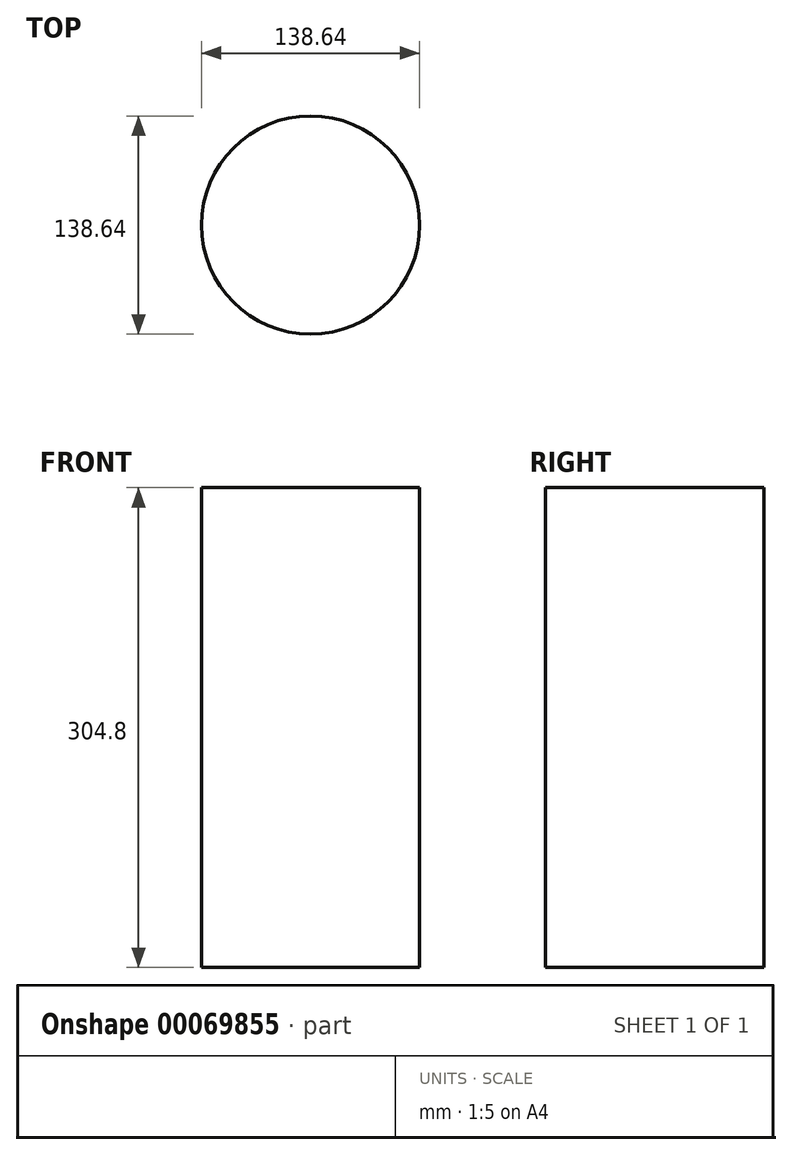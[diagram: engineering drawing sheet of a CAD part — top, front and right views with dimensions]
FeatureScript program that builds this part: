
annotation { "Feature Type Name" : "Feature", "Feature Type Description" : "" }
export const myFeature = defineFeature(function(context is Context, id is Id, definition is map)
    precondition{}
    {
        {
            var Q0;
            Q0=qCreatedBy(makeId("Top.planeOp"),FACE);
            var sketch = newSketch(context, id + "F0", { "sketchPlane" : qUnion([Q0])});
            skCircle(sketch, "E0", {"center": v(0, 0) * mm, "radius": 69.32 * mm});
            skSolve(sketch);
        }
        {
            var Q0;
            Q0=makeQuery(id+"F0.imprint","IMPRINT",FACE,{"disambiguationData":[TD([[makeQuery(id+"F0.imprint","IMPRINT",EDGE,{"derivedFrom":sQuery(id+"F0.wireOp",EDGE,"E0")}),1.0]])]});
            extrude(context, id + "F1", {"entities" : qUnion([Q0]), "oppositeDirection" : true, "depth" : 304.8 * mm});
        }
    });
